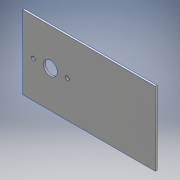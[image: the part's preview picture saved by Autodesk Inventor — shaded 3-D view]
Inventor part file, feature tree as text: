
AUTODESK INVENTOR PART (.ipt)
format: ipt  version: 2016 (Build 200138000, 138)  size: 125,440 bytes
history: native  units: mm
features: extrude x3, sketch x3, other x1
ambient origin geometry x8: Origin, YZ Plane, XZ Plane, XY Plane, X Axis, Y Axis, Z Axis, Center Point
bodies: Body1 (feature_tree)
feature tree (7):
  other  "ソリッド1"
  extrude  "押し出し1"  Depth=140.0mm
  extrude  "押し出し2"  Depth=80.0mm
  extrude  "押し出し3"  Depth=2.0mm TaperAngle=0.0deg
  sketch  "スケッチ1"
  sketch  "スケッチ2"
  sketch  "スケッチ3"
